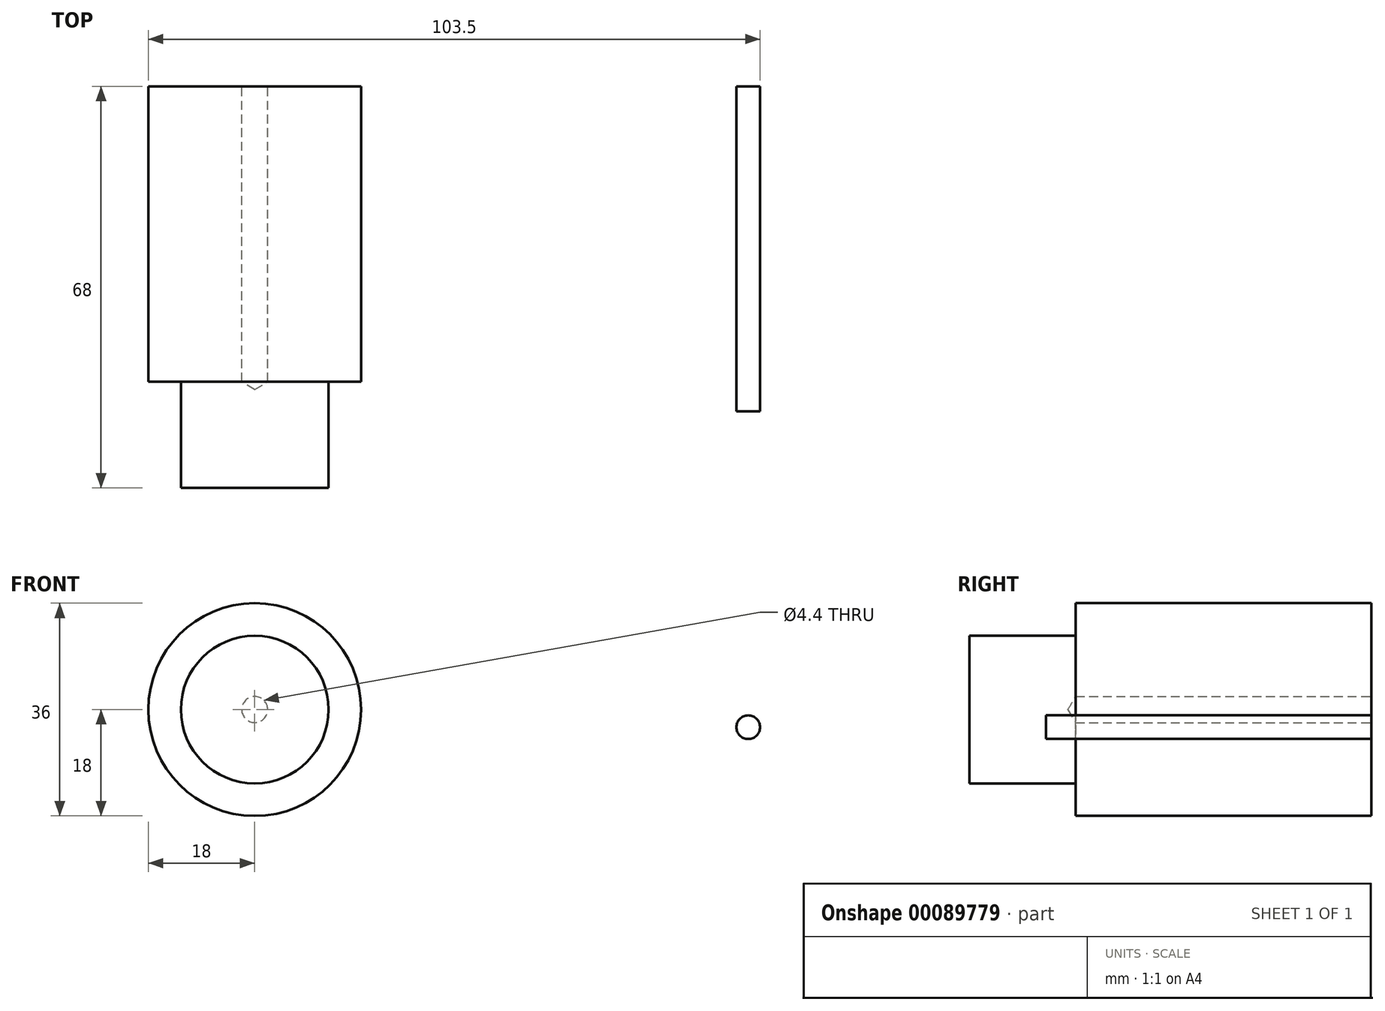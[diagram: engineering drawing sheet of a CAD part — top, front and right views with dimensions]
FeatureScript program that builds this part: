
annotation { "Feature Type Name" : "Feature", "Feature Type Description" : "" }
export const myFeature = defineFeature(function(context is Context, id is Id, definition is map)
    precondition{}
    {
        {
            var Q0;
            Q0=qCreatedBy(makeId("Front.planeOp"),FACE);
            var sketch = newSketch(context, id + "F0", { "sketchPlane" : qUnion([Q0])});
            skCircle(sketch, "E0", {"center": v(0, 0) * mm, "radius": 18 * mm});
            skSolve(sketch);
        }
        {
            var Q0;
            Q0=makeQuery(id+"F0.imprint","IMPRINT",FACE,{"disambiguationData":[TD([[makeQuery(id+"F0.imprint","IMPRINT",EDGE,{"derivedFrom":sQuery(id+"F0.wireOp",EDGE,"E0")}),1.0]])]});
            extrude(context, id + "F1", {"entities" : qUnion([Q0]), "depth" : 50 * mm});
        }
        {
            var Q0;
            Q0=makeQuery(id+"F1.opExtrude","CAP_FACE",FACE,{"disambiguationData":[OSD([sQuery(id+"F0.wireOp",EDGE,"E0")])],"isStart":false});
            var sketch = newSketch(context, id + "F2", { "sketchPlane" : qUnion([Q0])});
            skCircle(sketch, "E1", {"center": v(0, 0) * mm, "radius": 12.5 * mm});
            skSolve(sketch);
        }
        {
            var Q0;
            Q0=makeQuery(id+"F2.imprint","IMPRINT",FACE,{"disambiguationData":[TD([[makeQuery(id+"F2.imprint","IMPRINT",EDGE,{"derivedFrom":sQuery(id+"F2.wireOp",EDGE,"E1")}),1.0]])]});
            extrude(context, id + "F3", {"entities" : qUnion([Q0]), "operationType" : NewBodyOperationType.ADD, "depth" : 18 * mm});
        }
        {
            var Q0;
            Q0=makeQuery(id+"F1.opExtrude","CAP_FACE",FACE,{"disambiguationData":[OSD([sQuery(id+"F0.wireOp",EDGE,"E0")])],"isStart":true});
            var sketch = newSketch(context, id + "F4", { "sketchPlane" : qUnion([Q0])});
            skCircle(sketch, "E2", {"center": v(0, 0) * mm, "radius": 1.95 * mm});
            skSolve(sketch);
        }
        {
            var Q0;
            Q0=sQuery(id+"F4.wireOp",VERTEX,"E2.center");
            var Q1;
            Q1=makeQuery(id+"F1.opExtrude","SWEPT_BODY",BODY,{"disambiguationData":[OSD([sQuery(id+"F0.wireOp",EDGE,"E0")])]});
            hole(context, id + "F5", {"style" : HoleStyle.SIMPLE, "endStyle" : HoleEndStyle.BLIND, "standardTappedOrClearance" : lookupTablePath({ "standard" : "ISO", "fit" : "Normal", "size" : "M4", "type" : "Clearance" }), "standardBlindInLast" : lookupTablePath({ "fit" : "Standard", "standard" : "ISO", "size" : "M4", "type" : "Clearance" }), "holeDiameter" : 4.4 * mm, "holeDepth" : 50 * mm, "locations" : qUnion([Q0]), "scope" : qUnion([Q1])});
        }
        {
            var Q0;
            Q0=qCreatedBy(makeId("Front.planeOp"),FACE);
            var sketch = newSketch(context, id + "F6", { "sketchPlane" : qUnion([Q0])});
            skCircle(sketch, "E3", {"center": v(83.5, -2.98) * mm, "radius": 2 * mm});
            skSolve(sketch);
        }
        {
            var Q0;
            Q0=makeQuery(id+"F6.imprint","IMPRINT",FACE,{"disambiguationData":[TD([[makeQuery(id+"F6.imprint","IMPRINT",EDGE,{"derivedFrom":sQuery(id+"F6.wireOp",EDGE,"E3")}),1.0]])]});
            extrude(context, id + "F7", {"entities" : qUnion([Q0]), "depth" : 55 * mm});
        }
    });
